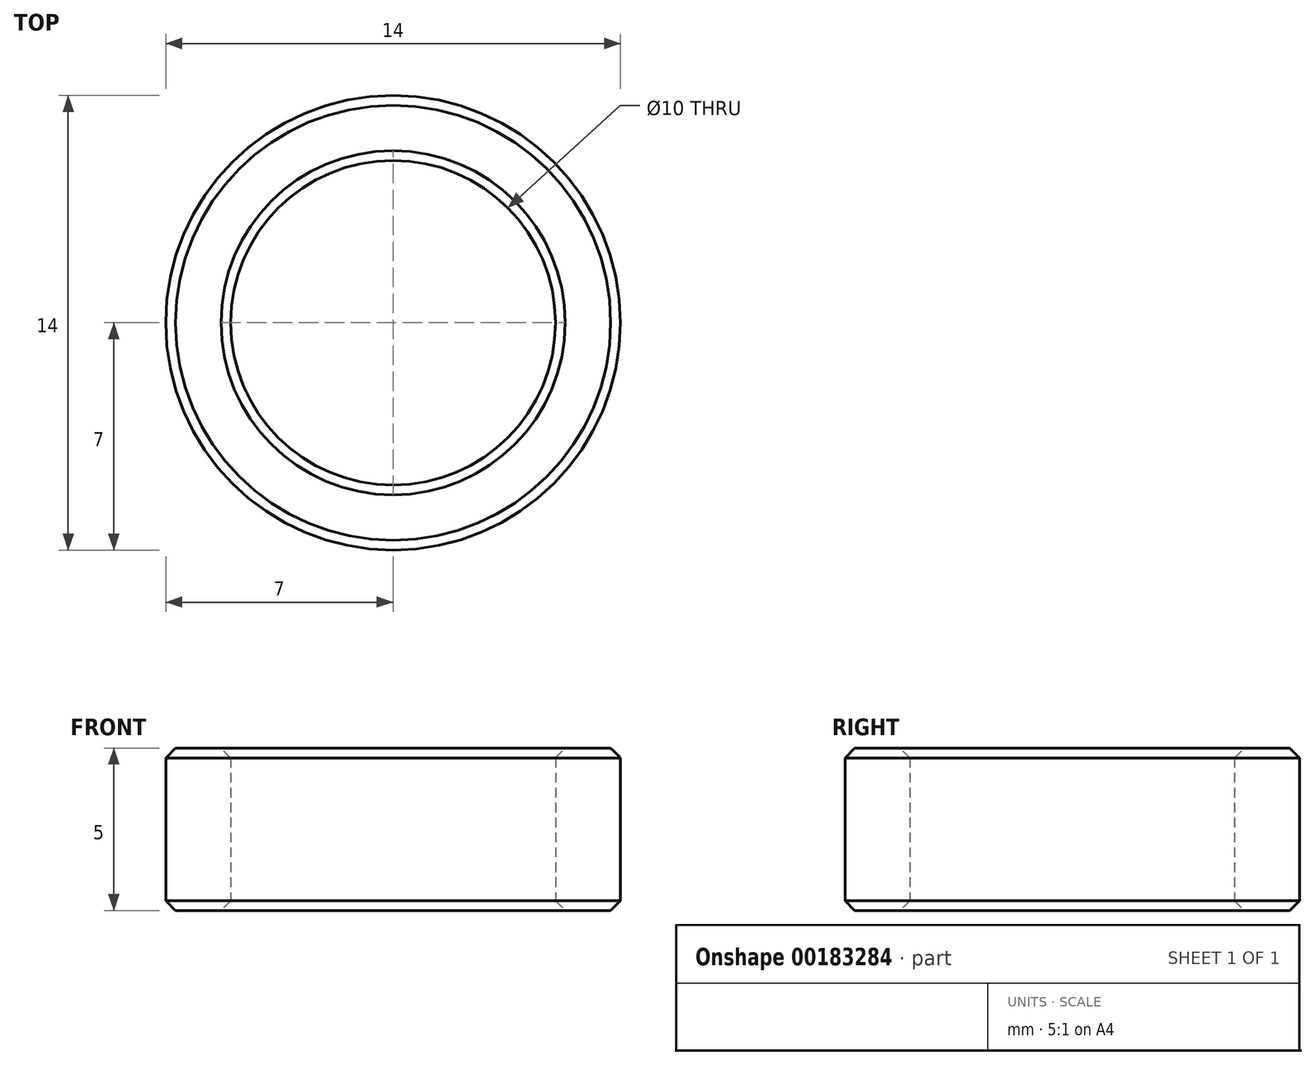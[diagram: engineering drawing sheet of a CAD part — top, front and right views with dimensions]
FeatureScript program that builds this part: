
annotation { "Feature Type Name" : "Feature", "Feature Type Description" : "" }
export const myFeature = defineFeature(function(context is Context, id is Id, definition is map)
    precondition{}
    {
        {
            var Q0;
            Q0=qCreatedBy(makeId("Top.planeOp"),FACE);
            var sketch = newSketch(context, id + "F0", { "sketchPlane" : qUnion([Q0])});
            skCircle(sketch, "E0", {"center": v(0, 0) * mm, "radius": 5 * mm});
            skCircle(sketch, "E1", {"center": v(0, 0) * mm, "radius": 7 * mm});
            skSolve(sketch);
        }
        {
            var Q0;
            Q0 = qSketchRegion(id + "F0", true);
            extrude(context, id + "F1", {"entities" : qUnion([Q0]), "endBound" : BoundingType.SYMMETRIC, "depth" : 5 * mm});
        }
        {
            var Q0;
            Q0=makeQuery(id+"F1.opExtrude","CAP_EDGE",EDGE,{"disambiguationData":[OSD([sQuery(id+"F0.wireOp",EDGE,"E1")])],"isStart":false});
            var Q1;
            Q1=makeQuery(id+"F1.opExtrude","CAP_EDGE",EDGE,{"disambiguationData":[OSD([sQuery(id+"F0.wireOp",EDGE,"E0")])],"isStart":false});
            var Q2;
            Q2=makeQuery(id+"F1.opExtrude","CAP_EDGE",EDGE,{"disambiguationData":[OSD([sQuery(id+"F0.wireOp",EDGE,"E1")])],"isStart":true});
            var Q3;
            Q3=makeQuery(id+"F1.opExtrude","CAP_EDGE",EDGE,{"disambiguationData":[OSD([sQuery(id+"F0.wireOp",EDGE,"E0")])],"isStart":true});
            chamfer(context, id + "F2", {"entities" : qUnion([Q0, Q1, Q2, Q3]), "width" : 0.3 * mm, "tangentPropagation" : true});
        }
    });
